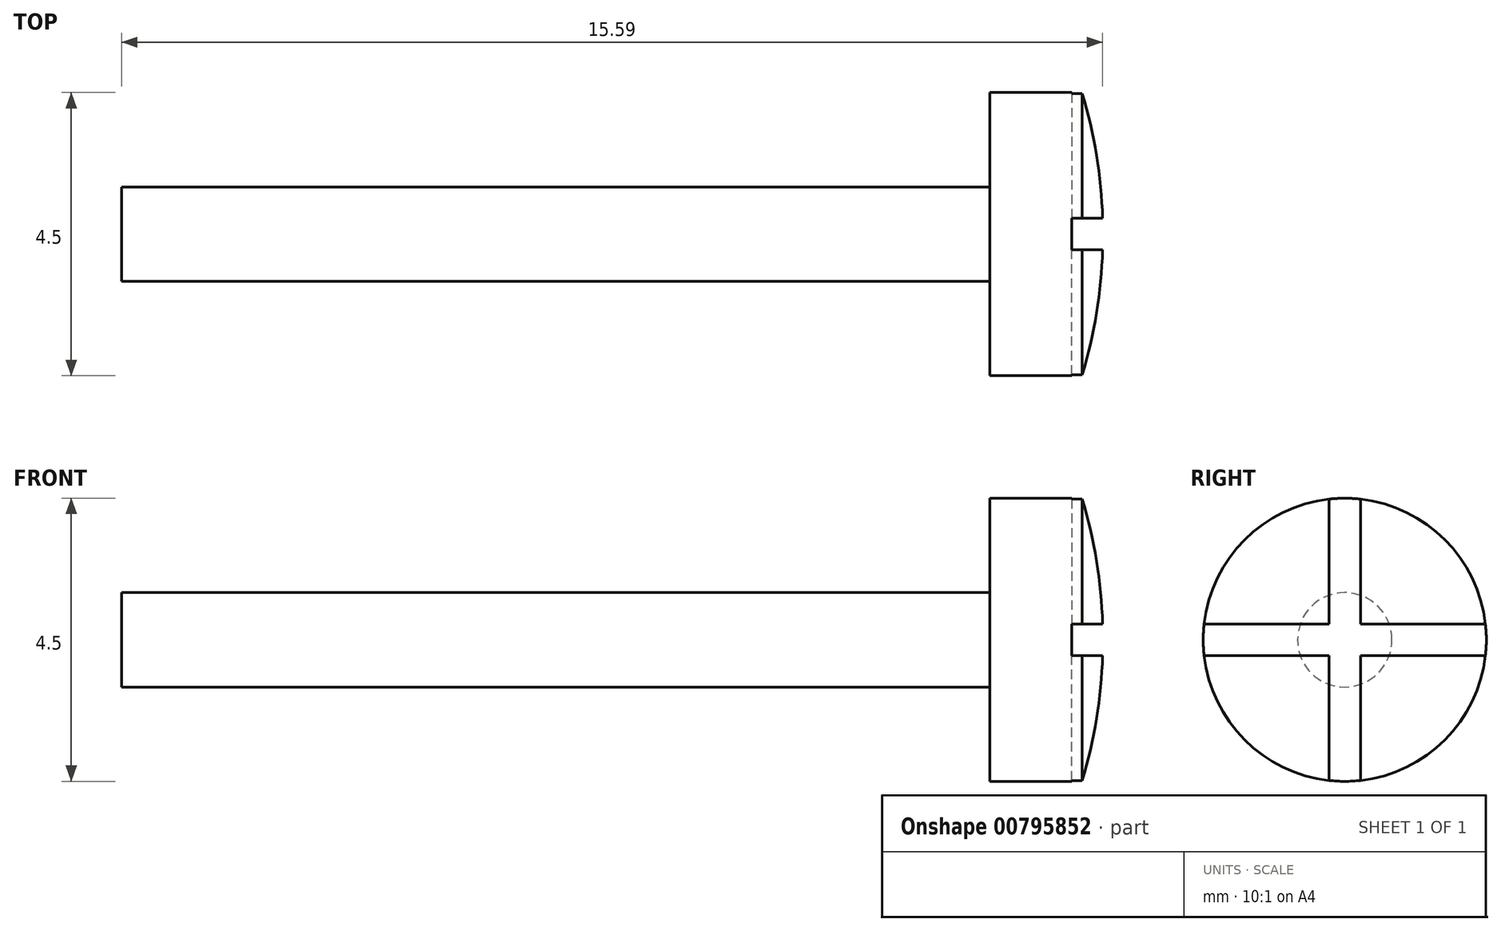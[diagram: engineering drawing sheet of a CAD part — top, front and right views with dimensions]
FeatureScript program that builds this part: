
annotation { "Feature Type Name" : "Feature", "Feature Type Description" : "" }
export const myFeature = defineFeature(function(context is Context, id is Id, definition is map)
    precondition{}
    {
        {
            var Q0;
            Q0=qCreatedBy(makeId("Top.planeOp"),FACE);
            var sketch = newSketch(context, id + "F0", { "sketchPlane" : qUnion([Q0])});
            skLineSegment(sketch, "E0", {"start": v(-16.09, 0) * mm, "end": v(19.15, 0) * mm, "construction": true});
            skLineSegment(sketch, "E1", {"start": v(-7.8, 0) * mm, "end": v(-7.8, 0.75) * mm});
            skLineSegment(sketch, "E2", {"start": v(-7.8, 0.75) * mm, "end": v(6, 0.75) * mm});
            skLineSegment(sketch, "E3", {"start": v(6, 0.75) * mm, "end": v(6, 2.25) * mm});
            skLineSegment(sketch, "E4", {"start": v(6, 2.25) * mm, "end": v(7.47, 2.25) * mm});
            skArc(sketch, "E5", {"start": v(7.47, 2.25) * mm, "mid": v(7.72, 1.14) * mm, "end": v(7.8, 0) * mm});
            skLineSegment(sketch, "E6", {"start": v(-7.8, 0) * mm, "end": v(7.8, 0) * mm});
            skSolve(sketch);
        }
        {
            var Q0;
            Q0 = qSketchRegion(id + "F0", true);
            var Q1;
            Q1=sQuery(id+"F0.wireOp",EDGE,"E0");
            revolve(context, id + "F1", {"surfaceOperationType" : NewSurfaceOperationType.NEW, "entities" : qUnion([Q0]), "axis" : qUnion([Q1]), "revolveType" : RevolveType.FULL});
        }
        {
            var Q0;
            Q0=qCreatedBy(makeId("Right.planeOp"),FACE);
            cPlane(context, id + "F2", {"entities" : qUnion([Q0]), "cplaneType" : CPlaneType.OFFSET, "offset" : 7.8 * mm, "width" : 150 * mm, "height" : 150 * mm});
        }
        {
            var Q0;
            Q0=qCreatedBy(id+"F2.planeOp",FACE);
            var sketch = newSketch(context, id + "F3", { "sketchPlane" : qUnion([Q0])});
            skLineSegment(sketch, "E7", {"start": v(0.25, 2.25) * mm, "end": v(0.25, 0.25) * mm});
            skLineSegment(sketch, "E8", {"start": v(0.25, 0.25) * mm, "end": v(2.25, 0.25) * mm});
            skLineSegment(sketch, "E9", {"start": v(2.25, 0.25) * mm, "end": v(2.25, -0.25) * mm});
            skLineSegment(sketch, "E10", {"start": v(2.25, -0.25) * mm, "end": v(0.25, -0.25) * mm});
            skLineSegment(sketch, "E11", {"start": v(0.25, -0.25) * mm, "end": v(0.25, -2.25) * mm});
            skLineSegment(sketch, "E12", {"start": v(0.25, -2.25) * mm, "end": v(-0.25, -2.25) * mm});
            skLineSegment(sketch, "E13", {"start": v(-0.25, -2.25) * mm, "end": v(-0.25, -0.25) * mm});
            skLineSegment(sketch, "E14", {"start": v(-0.25, -0.25) * mm, "end": v(-2.25, -0.25) * mm});
            skLineSegment(sketch, "E15", {"start": v(-2.25, -0.25) * mm, "end": v(-2.25, 0.25) * mm});
            skLineSegment(sketch, "E16", {"start": v(-2.25, 0.25) * mm, "end": v(-0.25, 0.25) * mm});
            skLineSegment(sketch, "E17", {"start": v(-0.25, 0.25) * mm, "end": v(-0.25, 2.25) * mm});
            skLineSegment(sketch, "E18", {"start": v(-0.25, 2.25) * mm, "end": v(0.25, 2.25) * mm});
            skSolve(sketch);
        }
        {
            var Q0;
            Q0 = qSketchRegion(id + "F3", true);
            extrude(context, id + "F4", {"entities" : qUnion([Q0]), "operationType" : NewBodyOperationType.REMOVE, "oppositeDirection" : true, "depth" : 0.5 * mm, "offsetDistance" : 25 * mm});
        }
    });
